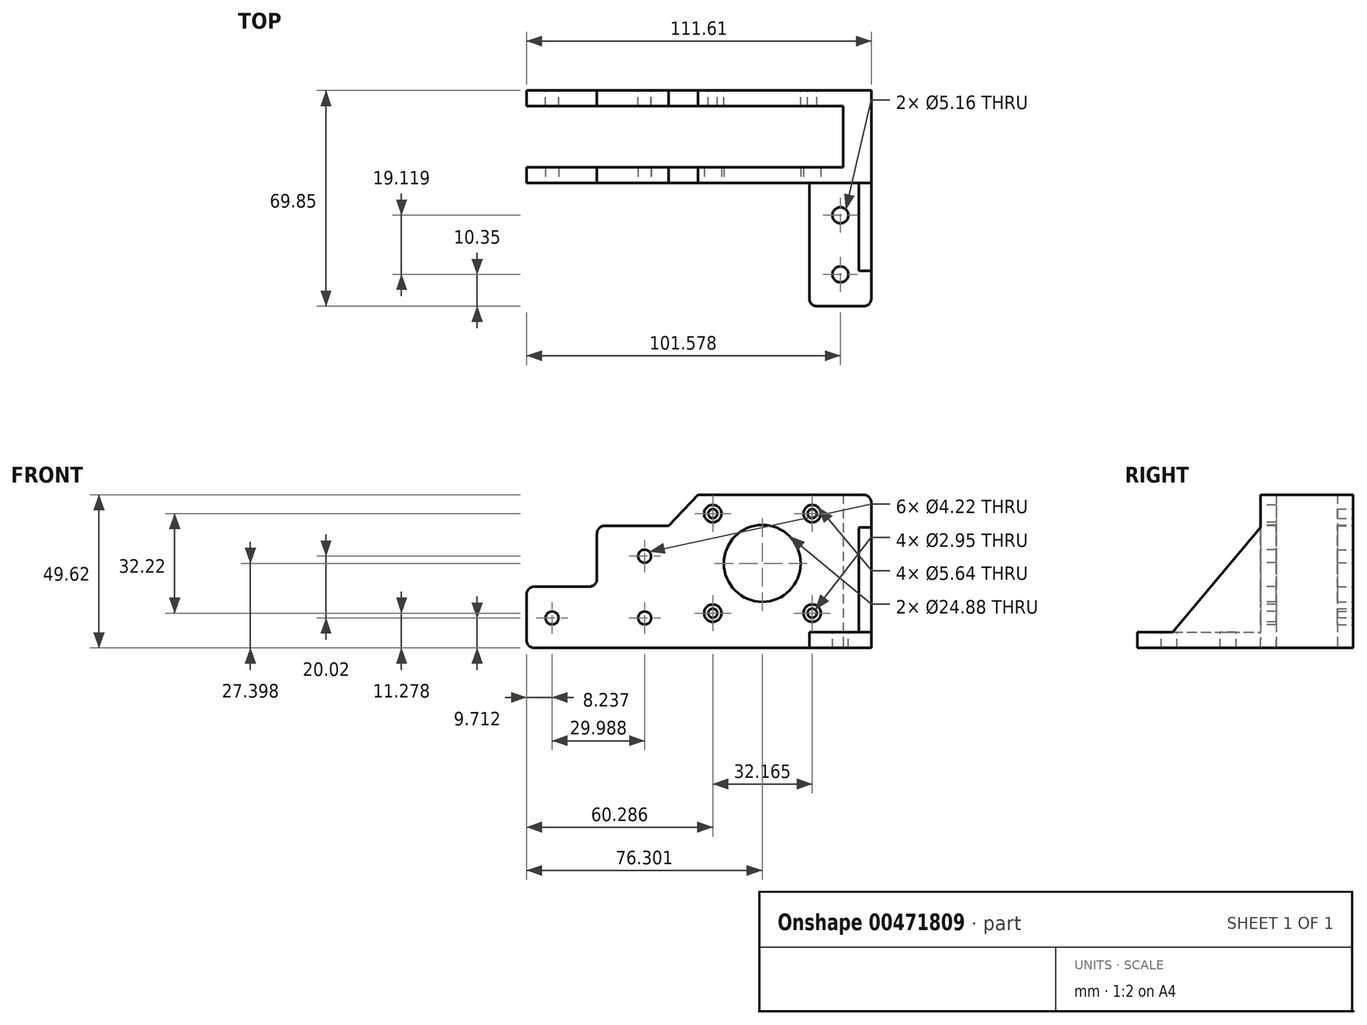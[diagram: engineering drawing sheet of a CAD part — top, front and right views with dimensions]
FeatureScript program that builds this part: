
annotation { "Feature Type Name" : "Feature", "Feature Type Description" : "" }
export const myFeature = defineFeature(function(context is Context, id is Id, definition is map)
    precondition{}
    {
        {
            var Q0;
            Q0=qCreatedBy(makeId("Front.planeOp"),FACE);
            var sketch = newSketch(context, id + "F0", { "sketchPlane" : qUnion([Q0])});
            skLineSegment(sketch, "E0", {"start": v(-36.49, 10.14) * mm, "end": v(-36.49, -9.57) * mm});
            skLineSegment(sketch, "E1", {"start": v(-36.49, -9.57) * mm, "end": v(-59.27, -9.57) * mm});
            skLineSegment(sketch, "E2", {"start": v(-59.27, -9.57) * mm, "end": v(-59.27, -29.44) * mm});
            skLineSegment(sketch, "E3", {"start": v(-59.27, -29.44) * mm, "end": v(73.5, -29.44) * mm});
            skCircle(sketch, "E4", {"center": v(-21.07, 0.3) * mm, "radius": 2.1 * mm});
            skCircle(sketch, "E5", {"center": v(-21.05, -19.72) * mm, "radius": 2.1 * mm});
            skCircle(sketch, "E6", {"center": v(-51.03, -19.73) * mm, "radius": 2.1 * mm});
            skLineSegment(sketch, "E7", {"start": v(52.34, 20.18) * mm, "end": v(-3.74, 20.18) * mm});
            skLineSegment(sketch, "E8", {"start": v(-3.74, 20.18) * mm, "end": v(-13.36, 10.14) * mm});
            skLineSegment(sketch, "E9", {"start": v(-13.36, 10.14) * mm, "end": v(-36.49, 10.14) * mm});
            skLineSegment(sketch, "E10", {"start": v(52.34, 20.18) * mm, "end": v(52.34, -29.44) * mm});
            skCircle(sketch, "E11", {"center": v(17.03, -2.04) * mm, "radius": 12.44 * mm});
            skCircle(sketch, "E12", {"center": v(1.02, 14.06) * mm, "radius": 1.48 * mm});
            skLineSegment(sketch, "E13.bottom", {"start": v(1.02, 14.06) * mm, "end": v(33.18, 14.06) * mm});
            skLineSegment(sketch, "E13.top", {"start": v(1.02, -18.16) * mm, "end": v(33.18, -18.16) * mm});
            skLineSegment(sketch, "E13.left", {"start": v(1.02, 14.06) * mm, "end": v(1.02, -18.16) * mm});
            skLineSegment(sketch, "E13.right", {"start": v(33.18, 14.06) * mm, "end": v(33.18, -18.16) * mm});
            skCircle(sketch, "E14", {"center": v(33.18, 14.06) * mm, "radius": 1.48 * mm});
            skCircle(sketch, "E15", {"center": v(33.18, -18.16) * mm, "radius": 1.48 * mm});
            skCircle(sketch, "E16", {"center": v(1.02, -18.16) * mm, "radius": 1.48 * mm});
            skSolve(sketch);
        }
        {
            var Q0;
            Q0 = qSketchRegion(id + "F0", true);
            var Q1;
            Q1=makeQuery(id+"F0.imprint","IMPRINT",FACE,{"disambiguationData":[TD([[makeQuery(id+"F0.imprint","IMPRINT",EDGE,{"derivedFrom":sQuery(id+"F0.wireOp",EDGE,"E11")}),-1.0]])]});
            extrude(context, id + "F1", {"entities" : qUnion([Q0, Q1]), "depth" : 5.08 * mm});
        }
        {
            var Q0;
            Q0=makeQuery(id+"F1.opExtrude","CAP_FACE",FACE,{"disambiguationData":[OSD([sQuery(id+"F0.wireOp",EDGE,"E0"),sQuery(id+"F0.wireOp",EDGE,"E1"),sQuery(id+"F0.wireOp",EDGE,"E2"),sQuery(id+"F0.wireOp",EDGE,"E3"),sQuery(id+"F0.wireOp",EDGE,"E4"),sQuery(id+"F0.wireOp",EDGE,"E5"),sQuery(id+"F0.wireOp",EDGE,"E6"),sQuery(id+"F0.wireOp",EDGE,"E7"),sQuery(id+"F0.wireOp",EDGE,"E8"),sQuery(id+"F0.wireOp",EDGE,"E9"),sQuery(id+"F0.wireOp",EDGE,"E10"),sQuery(id+"F0.wireOp",EDGE,"E11"),sQuery(id+"F0.wireOp",EDGE,"E12"),sQuery(id+"F0.wireOp",EDGE,"E14"),sQuery(id+"F0.wireOp",EDGE,"E15"),sQuery(id+"F0.wireOp",EDGE,"E16")])],"isStart":false});
            var sketch = newSketch(context, id + "F2", { "sketchPlane" : qUnion([Q0])});
            skLineSegment(sketch, "E17.bottom", {"start": v(52.34, 20.18) * mm, "end": v(43.18, 20.18) * mm});
            skLineSegment(sketch, "E17.top", {"start": v(52.34, -29.44) * mm, "end": v(43.18, -29.44) * mm});
            skLineSegment(sketch, "E17.left", {"start": v(52.34, 20.18) * mm, "end": v(52.34, -29.44) * mm});
            skLineSegment(sketch, "E17.right", {"start": v(43.18, 20.18) * mm, "end": v(43.18, -29.44) * mm});
            skSolve(sketch);
        }
        {
            var Q0;
            Q0 = qSketchRegion(id + "F2", true);
            extrude(context, id + "F3", {"entities" : qUnion([Q0]), "operationType" : NewBodyOperationType.ADD, "depth" : 9.9 * mm});
        }
        {
            var Q0;
            Q0=makeQuery(id+"F3.opExtrude","CAP_FACE",FACE,{"disambiguationData":[OSD([sQuery(id+"F2.wireOp",EDGE,"E17.bottom"),sQuery(id+"F2.wireOp",EDGE,"E17.top"),sQuery(id+"F2.wireOp",EDGE,"E17.left"),sQuery(id+"F2.wireOp",EDGE,"E17.right")])],"isStart":false});
            cPlane(context, id + "F4", {"entities" : qUnion([Q0]), "cplaneType" : CPlaneType.OFFSET, "offset" : 0 * mm, "width" : 152.4 * mm, "height" : 152.4 * mm});
        }
        {
            var Q0;
            Q0=makeQuery(id+"F1.opExtrude","SWEPT_BODY",BODY,{"disambiguationData":[OSD([sQuery(id+"F0.wireOp",EDGE,"E0"),sQuery(id+"F0.wireOp",EDGE,"E1"),sQuery(id+"F0.wireOp",EDGE,"E2"),sQuery(id+"F0.wireOp",EDGE,"E3"),sQuery(id+"F0.wireOp",EDGE,"E4"),sQuery(id+"F0.wireOp",EDGE,"E5"),sQuery(id+"F0.wireOp",EDGE,"E6"),sQuery(id+"F0.wireOp",EDGE,"E7"),sQuery(id+"F0.wireOp",EDGE,"E8"),sQuery(id+"F0.wireOp",EDGE,"E9"),sQuery(id+"F0.wireOp",EDGE,"E10"),sQuery(id+"F0.wireOp",EDGE,"E11"),sQuery(id+"F0.wireOp",EDGE,"E12"),sQuery(id+"F0.wireOp",EDGE,"E14"),sQuery(id+"F0.wireOp",EDGE,"E15"),sQuery(id+"F0.wireOp",EDGE,"E16")])]});
            var Q1;
            Q1=qCreatedBy(id+"F4.planeOp",FACE);
            mirror(context, id + "F5", {"operationType" : NewBodyOperationType.ADD, "entities" : qUnion([Q0]), "mirrorPlane" : qUnion([Q1])});
        }
        {
            var Q0;
            Q0=makeQuery(id+"F5.opPattern","COPY",FACE,{"derivedFrom":makeQuery(id+"F1.opExtrude","CAP_FACE",FACE,{"disambiguationData":[OSD([sQuery(id+"F0.wireOp",EDGE,"E0"),sQuery(id+"F0.wireOp",EDGE,"E1"),sQuery(id+"F0.wireOp",EDGE,"E2"),sQuery(id+"F0.wireOp",EDGE,"E3"),sQuery(id+"F0.wireOp",EDGE,"E4"),sQuery(id+"F0.wireOp",EDGE,"E5"),sQuery(id+"F0.wireOp",EDGE,"E6"),sQuery(id+"F0.wireOp",EDGE,"E7"),sQuery(id+"F0.wireOp",EDGE,"E8"),sQuery(id+"F0.wireOp",EDGE,"E9"),sQuery(id+"F0.wireOp",EDGE,"E10"),sQuery(id+"F0.wireOp",EDGE,"E11"),sQuery(id+"F0.wireOp",EDGE,"E12"),sQuery(id+"F0.wireOp",EDGE,"E14"),sQuery(id+"F0.wireOp",EDGE,"E15"),sQuery(id+"F0.wireOp",EDGE,"E16")])],"isStart":true}),"instanceName":"1"});
            var sketch = newSketch(context, id + "F6", { "sketchPlane" : qUnion([Q0])});
            skLineSegment(sketch, "E18.bottom", {"start": v(52.34, -29.44) * mm, "end": v(32.28, -29.44) * mm});
            skLineSegment(sketch, "E18.top", {"start": v(52.34, -24.36) * mm, "end": v(32.28, -24.36) * mm});
            skLineSegment(sketch, "E18.left", {"start": v(52.34, -29.44) * mm, "end": v(52.34, -24.36) * mm});
            skLineSegment(sketch, "E18.right", {"start": v(32.28, -29.44) * mm, "end": v(32.28, -24.36) * mm});
            skSolve(sketch);
        }
        {
            var Q0;
            Q0 = qSketchRegion(id + "F6", true);
            extrude(context, id + "F7", {"entities" : qUnion([Q0]), "operationType" : NewBodyOperationType.ADD, "depth" : 39.88 * mm});
        }
        {
            var Q0;
            Q0=makeQuery(id+"F5.opPattern","COPY",FACE,{"derivedFrom":makeQuery(id+"F1.opExtrude","CAP_FACE",FACE,{"disambiguationData":[OSD([sQuery(id+"F0.wireOp",EDGE,"E0"),sQuery(id+"F0.wireOp",EDGE,"E1"),sQuery(id+"F0.wireOp",EDGE,"E2"),sQuery(id+"F0.wireOp",EDGE,"E3"),sQuery(id+"F0.wireOp",EDGE,"E4"),sQuery(id+"F0.wireOp",EDGE,"E5"),sQuery(id+"F0.wireOp",EDGE,"E6"),sQuery(id+"F0.wireOp",EDGE,"E7"),sQuery(id+"F0.wireOp",EDGE,"E8"),sQuery(id+"F0.wireOp",EDGE,"E9"),sQuery(id+"F0.wireOp",EDGE,"E10"),sQuery(id+"F0.wireOp",EDGE,"E11"),sQuery(id+"F0.wireOp",EDGE,"E12"),sQuery(id+"F0.wireOp",EDGE,"E14"),sQuery(id+"F0.wireOp",EDGE,"E15"),sQuery(id+"F0.wireOp",EDGE,"E16")])],"isStart":true}),"instanceName":"1"});
            var sketch = newSketch(context, id + "F8", { "sketchPlane" : qUnion([Q0])});
            skCircle(sketch, "E19", {"center": v(1.02, 14.06) * mm, "radius": 2.82 * mm});
            skCircle(sketch, "E20", {"center": v(1.02, -18.16) * mm, "radius": 2.82 * mm});
            skCircle(sketch, "E21", {"center": v(33.18, -18.16) * mm, "radius": 2.82 * mm});
            skCircle(sketch, "E22", {"center": v(33.18, 14.06) * mm, "radius": 2.82 * mm});
            skSolve(sketch);
        }
        {
            var Q0;
            Q0 = qSketchRegion(id + "F8", true);
            extrude(context, id + "F9", {"entities" : qUnion([Q0]), "operationType" : NewBodyOperationType.REMOVE, "oppositeDirection" : true, "depth" : 20.07 * mm});
        }
        {
            var Q0;
            Q0=makeQuery(id+"F1.opExtrude","SWEPT_EDGE",EDGE,{"disambiguationData":[OSD([sQuery(id+"F0.wireOp",EDGE,"E1"),sQuery(id+"F0.wireOp",EDGE,"E2")])]});
            var Q1;
            Q1=makeQuery(id+"F5.opPattern","COPY",EDGE,{"derivedFrom":makeQuery(id+"F1.opExtrude","SWEPT_EDGE",EDGE,{"disambiguationData":[OSD([sQuery(id+"F0.wireOp",EDGE,"E1"),sQuery(id+"F0.wireOp",EDGE,"E2")])]}),"instanceName":"1"});
            var Q2;
            Q2=makeQuery(id+"F1.opExtrude","SWEPT_EDGE",EDGE,{"disambiguationData":[OSD([sQuery(id+"F0.wireOp",EDGE,"E0"),sQuery(id+"F0.wireOp",EDGE,"E1")])]});
            var Q3;
            Q3=makeQuery(id+"F1.opExtrude","SWEPT_EDGE",EDGE,{"disambiguationData":[OSD([sQuery(id+"F0.wireOp",EDGE,"E0"),sQuery(id+"F0.wireOp",EDGE,"E9")])]});
            var Q4;
            Q4=makeQuery(id+"F5.opPattern","COPY",EDGE,{"derivedFrom":makeQuery(id+"F1.opExtrude","SWEPT_EDGE",EDGE,{"disambiguationData":[OSD([sQuery(id+"F0.wireOp",EDGE,"E0"),sQuery(id+"F0.wireOp",EDGE,"E9")])]}),"instanceName":"1"});
            var Q5;
            Q5=makeQuery(id+"F5.opPattern","COPY",EDGE,{"derivedFrom":makeQuery(id+"F1.opExtrude","SWEPT_EDGE",EDGE,{"disambiguationData":[OSD([sQuery(id+"F0.wireOp",EDGE,"E0"),sQuery(id+"F0.wireOp",EDGE,"E1")])]}),"instanceName":"1"});
            var Q6;
            Q6=makeQuery(id+"F1.opExtrude","SWEPT_EDGE",EDGE,{"disambiguationData":[OSD([sQuery(id+"F0.wireOp",EDGE,"E2"),sQuery(id+"F0.wireOp",EDGE,"E3")])]});
            var Q7;
            Q7=makeQuery(id+"F5.opPattern","COPY",EDGE,{"derivedFrom":makeQuery(id+"F1.opExtrude","SWEPT_EDGE",EDGE,{"disambiguationData":[OSD([sQuery(id+"F0.wireOp",EDGE,"E2"),sQuery(id+"F0.wireOp",EDGE,"E3")])]}),"instanceName":"1"});
            var Q8;
            Q8=makeQuery(id+"F7.opExtrude","CAP_EDGE",EDGE,{"disambiguationData":[OSD([sQuery(id+"F6.wireOp",EDGE,"E18.right")])],"isStart":false});
            var Q9;
            Q9=makeQuery(id+"F7.opExtrude","CAP_EDGE",EDGE,{"disambiguationData":[OSD([sQuery(id+"F6.wireOp",EDGE,"E18.left")])],"isStart":false});
            fillet(context, id + "F10", {"entities" : qUnion([Q0, Q1, Q2, Q3, Q4, Q5, Q6, Q7, Q8, Q9]), "radius" : 2.54 * mm, "tangentPropagation" : true, "allowEdgeOverflow" : false});
        }
        {
            var Q0;
            {var subQ0=makeQuery(id+"F3.boolean.opBoolean","MERGE",FACE,{"derivedFrom":[makeQuery(id+"F1.opExtrude","SWEPT_FACE",FACE,{"disambiguationData":[OSD([sQuery(id+"F0.wireOp",EDGE,"E10")])]}),makeQuery(id+"F3.opExtrude","SWEPT_FACE",FACE,{"disambiguationData":[OSD([sQuery(id+"F2.wireOp",EDGE,"E17.left")])]})]});Q0=makeQuery(id+"F7.boolean.opBoolean","MERGE",FACE,{"derivedFrom":[makeQuery(id+"F5.boolean.opBoolean","MERGE",FACE,{"derivedFrom":[subQ0,makeQuery(id+"F5.opPattern","COPY",FACE,{"derivedFrom":subQ0,"instanceName":"1"})]}),makeQuery(id+"F7.opExtrude","SWEPT_FACE",FACE,{"disambiguationData":[OSD([sQuery(id+"F6.wireOp",EDGE,"E18.left")])]})]});}
            var sketch = newSketch(context, id + "F11", { "sketchPlane" : qUnion([Q0])});
            skLineSegment(sketch, "E23", {"start": v(-48.64, -24.36) * mm, "end": v(-29.97, -2.09) * mm});
            skLineSegment(sketch, "E24", {"start": v(-58.4, -24.36) * mm, "end": v(-29.97, 9.56) * mm});
            skSolve(sketch);
        }
        {
            var Q0;
            {var subQ0=sQuery(id+"F11.wireOp",EDGE,"E23");Q0=makeQuery(id+"F11.imprint","IMPRINT",FACE,{"disambiguationData":[TD([[makeQuery(id+"F11.imprint","IMPRINT",EDGE,{"derivedFrom":subQ0}),-1.0]])]});}
            var Q1;
            {var subQ0=sQuery(id+"F11.wireOp",EDGE,"E23");Q1=makeQuery(id+"F11.imprint","IMPRINT",FACE,{"disambiguationData":[TD([[makeQuery(id+"F11.imprint","IMPRINT",EDGE,{"derivedFrom":subQ0}),1.0]])]});}
            extrude(context, id + "F12", {"entities" : qUnion([Q0, Q1]), "operationType" : NewBodyOperationType.ADD, "oppositeDirection" : true, "depth" : 4.06 * mm});
        }
        {
            var Q0;
            Q0=makeQuery(id+"F7.opExtrude","SWEPT_FACE",FACE,{"disambiguationData":[OSD([sQuery(id+"F6.wireOp",EDGE,"E18.top")])]});
            var sketch = newSketch(context, id + "F13", { "sketchPlane" : qUnion([Q0])});
            skLineSegment(sketch, "E25", {"start": v(32.28, -62.45) * mm, "end": v(52.34, -62.45) * mm});
            skLineSegment(sketch, "E26", {"start": v(42.3, -62.45) * mm, "end": v(42.3, -34.77) * mm});
            skCircle(sketch, "E27", {"center": v(42.3, -40.38) * mm, "radius": 2.58 * mm});
            skCircle(sketch, "E28", {"center": v(42.3, -59.5) * mm, "radius": 2.58 * mm});
            skSolve(sketch);
        }
        {
            var Q0;
            Q0 = qSketchRegion(id + "F13", true);
            extrude(context, id + "F14", {"entities" : qUnion([Q0]), "operationType" : NewBodyOperationType.REMOVE, "oppositeDirection" : true, "depth" : 25.4 * mm});
        }
        {
            var Q0;
            {var subQ0=makeQuery(id+"F3.boolean.opBoolean","MERGE",EDGE,{"derivedFrom":[makeQuery(id+"F1.opExtrude","SWEPT_EDGE",EDGE,{"disambiguationData":[OSD([sQuery(id+"F0.wireOp",EDGE,"E7"),sQuery(id+"F0.wireOp",EDGE,"E10")])]}),makeQuery(id+"F3.opExtrude","SWEPT_EDGE",EDGE,{"disambiguationData":[OSD([sQuery(id+"F2.wireOp",EDGE,"E17.bottom"),sQuery(id+"F2.wireOp",EDGE,"E17.left")])]})]});Q0=makeQuery(id+"F5.boolean.opBoolean","MERGE",EDGE,{"derivedFrom":[subQ0,makeQuery(id+"F5.opPattern","COPY",EDGE,{"derivedFrom":subQ0,"instanceName":"1"})]});}
            fillet(context, id + "F15", {"entities" : qUnion([Q0]), "radius" : 2.54 * mm, "tangentPropagation" : true, "allowEdgeOverflow" : false});
        }
    });
